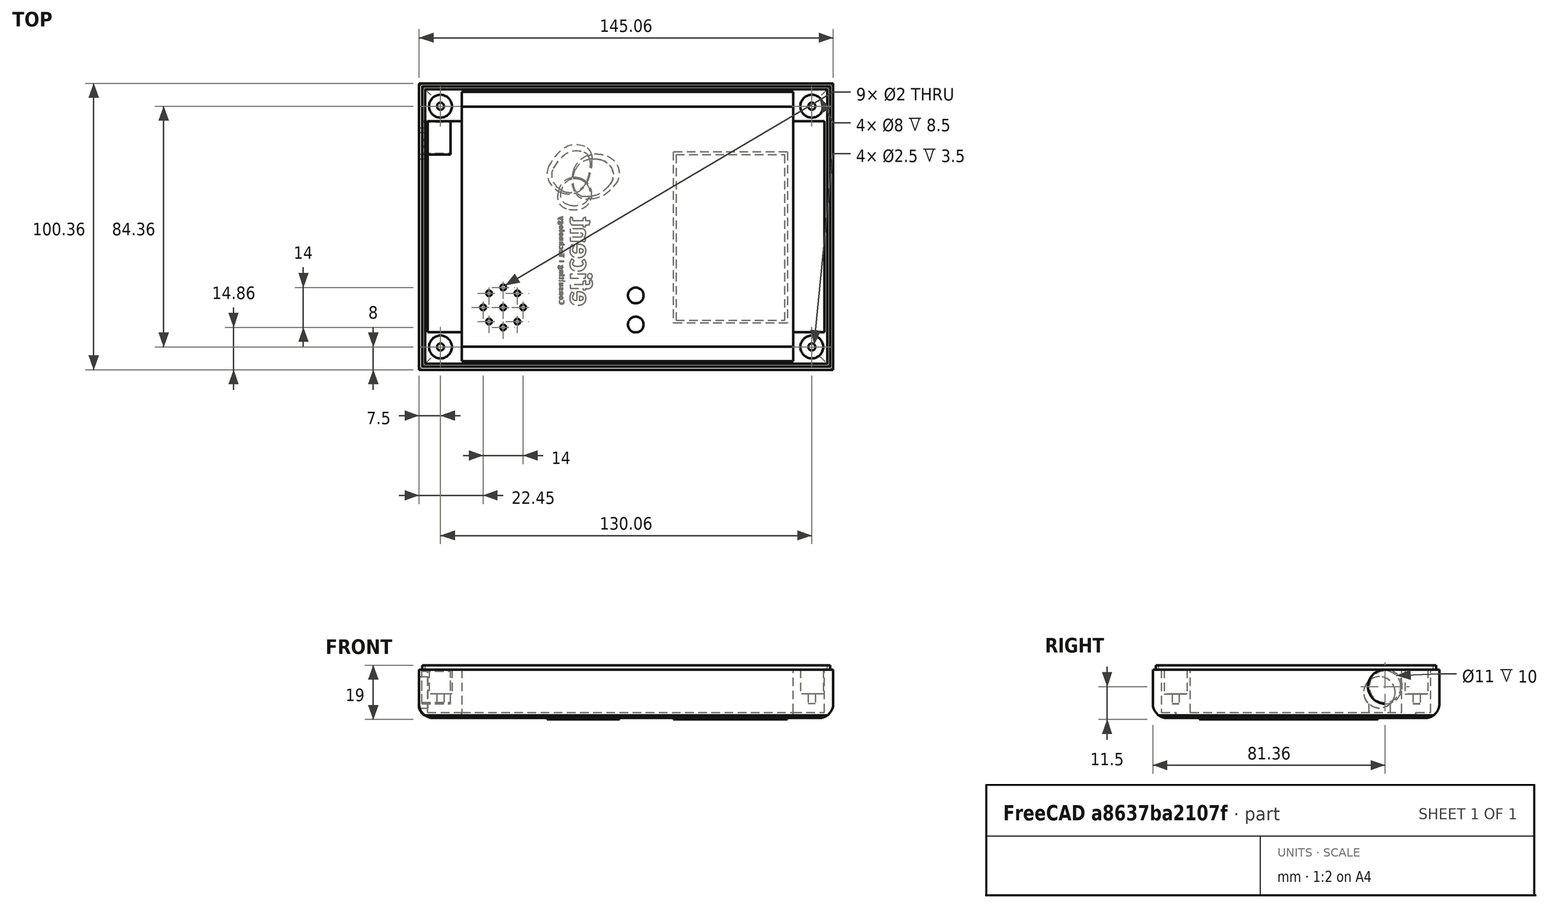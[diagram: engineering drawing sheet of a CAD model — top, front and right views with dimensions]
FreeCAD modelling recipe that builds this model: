
FCSTD DOCUMENT  (FreeCAD 0.16R6712 (Git))
Label: top_case_part1
License: All rights reserved
LicenseURL: http://en.wikipedia.org/wiki/All_rights_reserved
objects: Part::FeaturePython×63, Part::Extrusion×54, Part::Cut×48, Part::Box×31, Part::MultiFuse×27, Part::Cylinder×22, Part::Feature×5, Part::MultiCommon×3, Part::Fillet×2, App::MeasureDistance×1, Mesh::Feature×1
note: 255 computed .brp shape members not serialized (recipe doc carries the construction recipe); baked Part::Feature solids carry a one-line shape summary decoded from their .brp

FEATURE [Part::Box] Box005  label="top_case_master"
  Height = 17
  Length = 145.06
  Placement = pos=(-4,0,31) rot=(0,0,1;0rad)
  Width = 100.36
FEATURE [Part::Box] Box006  label="top_case_master_emptying"
  Height = 14
  Length = 116.06
  Placement = pos=(11,3,31) rot=(0,0,1;0rad)
  Width = 94.36
FEATURE [Part::Cut] Cut002  label="top_case_empty"
  Base = -> Box005
  Tool = -> Box006
FEATURE [Part::Cylinder] Cylinder002  label="hole_2_4"
  Angle = 360
  Height = 43
  Placement = pos=(3.5,8,0) rot=(0,0,1;0rad)
  Radius = 1.25
FEATURE [Part::FeaturePython] Array002  label="array_hole_2_4"  # Draft array (typed FeaturePython)
  Angle = 360
  ArrayType = 0
  Axis = (0,0,1)
  Base = -> Cylinder002
  Center = (0,0,0)
  Fuse = false
  IntervalAxis = (0,0,0)
  IntervalX = (130.06,0,0)
  IntervalY = (0,84.36,0)
  IntervalZ = (0,0,0)
  NumberPolar = 1
  NumberX = 2
  NumberY = 2
  NumberZ = 1
FEATURE [Part::Cut] Cut003  label="top_case_empty_witholes"
  Base = -> Cut002
  Tool = -> Array002
FEATURE [Part::Box] Box007  label="top_case_support_master"
  Height = 19.5
  Length = 7
  Placement = pos=(18.5,3,-10.5) rot=(0,0,1;0rad)
  Width = 7
FEATURE [Part::FeaturePython] Array003  label="array_top_case_support_master"  # Draft array (typed FeaturePython)
  Angle = 360
  ArrayType = 0
  Axis = (0,0,1)
  Base = -> Box007
  Center = (0,0,0)
  Fuse = false
  IntervalAxis = (0,0,0)
  IntervalX = (77.06,0,0)
  IntervalY = (0,87.36,0)
  IntervalZ = (0,0,0)
  NumberPolar = 1
  NumberX = 2
  NumberY = 2
  NumberZ = 1
  Placement = pos=(0,0,36) rot=(0,0,1;0rad)
FEATURE [Part::MultiFuse] Fusion004  label="top_case_withsupports"
  Placement = pos=(0,0,-16) rot=(0,0,1;0rad)
  Shapes = -> [Cut003,Array003]
FEATURE [Part::Cylinder] Cylinder003  label="hole_power_supply"
  Angle = 360
  Height = 19
  Placement = pos=(-5,21,23) rot=(0,1,0;1.5708rad)
  Radius = 5.5
FEATURE [Part::Cut] Cut004  label="top_case_with_power_supply_hole"
  Base = -> Fusion004
  Placement = pos=(0,0,21) rot=(0,0,1;0rad)
  Tool = -> Cylinder003
FEATURE [Part::Box] Box010  label="cierre_top_length_master"
  Height = 1.5
  Length = 142.76
  Placement = pos=(-2.9,1.1,34.5) rot=(0,0,1;0rad)
  Width = 1
FEATURE [Part::Box] Box011  label="cierre_top_width_master"
  Height = 1.5
  Length = 1
  Placement = pos=(-2.9,1.1,34.5) rot=(0,0,1;0rad)
  Width = 98.16
FEATURE [Part::FeaturePython] Array006  label="array_cierre_top_length"  # Draft array (typed FeaturePython)
  Angle = 360
  ArrayType = 0
  Axis = (0,0,1)
  Base = -> Box010
  Center = (0,0,0)
  Fuse = false
  IntervalAxis = (0,0,0)
  IntervalX = (1,0,0)
  IntervalY = (0,97.16,0)
  IntervalZ = (0,0,0)
  NumberPolar = 1
  NumberX = 1
  NumberY = 2
  NumberZ = 1
FEATURE [Part::FeaturePython] Array007  label="array_cierre_top_width"  # Draft array (typed FeaturePython)
  Angle = 360
  ArrayType = 0
  Axis = (0,0,1)
  Base = -> Box011
  Center = (0,0,0)
  Fuse = false
  IntervalAxis = (0,0,0)
  IntervalX = (141.86,0,0)
  IntervalY = (0,1,0)
  IntervalZ = (0,0,0)
  NumberPolar = 1
  NumberX = 2
  NumberY = 1
  NumberZ = 1
FEATURE [Part::MultiFuse] Fusion007
  Shapes = -> [Cut004,Array007]
FEATURE [Part::MultiFuse] Fusion008  label="top_case_with_border"
  Placement = pos=(0,0,2.5) rot=(0,0,1;0rad)
  Shapes = -> [Array006,Fusion007]
FEATURE [Part::Cylinder] Cylinder004  label="led2_hole_up"
  Angle = 360
  Height = 1
  Placement = pos=(71.9,84.5,52.5) rot=(0,0,1;0rad)
  Radius = 3
FEATURE [Part::Cylinder] Cylinder005  label="led1_hole_up"
  Angle = 360
  Height = 1
  Placement = pos=(71.9,74.3,52.5) rot=(0,0,1;0rad)
  Radius = 3
FEATURE [Part::Cut] Cut005
  Base = -> Fusion008
  Tool = -> Cylinder004
FEATURE [Part::Cut] Cut006  label="top_case_with_led_I"
  Base = -> Cut005
  Tool = -> Cylinder005
FEATURE [Part::Cylinder] Cylinder006  label="led1_hole_up001"
  Angle = 360
  Height = 4
  Placement = pos=(71.9,74.3,51.5) rot=(0,0,1;0rad)
  Radius = 2.75
FEATURE [Part::Cylinder] Cylinder007  label="led2_hole_up001"
  Angle = 360
  Height = 4
  Placement = pos=(71.9,84.5,51.5) rot=(0,0,1;0rad)
  Radius = 2.75
FEATURE [Part::Cut] Cut007
  Base = -> Cut006
  Tool = -> Cylinder006
FEATURE [Part::Cut] Cut008
  Base = -> Cut007
  Tool = -> Cylinder007
FEATURE [Part::Fillet] Fillet  label="top_case_bisel"
  Base = -> Cut008
  Edges = 4 edges r=5: [Edge2,Edge8,Edge9,Edge10]
FEATURE [Part::Box] Box012  label="slot_for_rfid"
  Height = 1
  Length = 40
  Placement = pos=(85,24,54.5) rot=(0,0,1;0rad)
  Width = 60
FEATURE [Part::Cut] Cut009  label="top_case_slot_rfid"
  Base = -> Fillet
  Tool = -> Box012
FEATURE [Part::Cylinder] Cylinder008  label="slot_for_buzzer"
  Angle = 360
  Height = 1
  Placement = pos=(39.4,79.4,54.5) rot=(0,0,1;0rad)
  Radius = 11
FEATURE [Part::Cylinder] Cylinder009  label="miniholes_buzzer_center"
  Angle = 360
  Height = 10
  Placement = pos=(25.446,78.5,49.5) rot=(0,0,1;0rad)
  Radius = 1
FEATURE [Part::Cylinder] Cylinder010  label="miniholes_buzzer_master"
  Angle = 360
  Height = 10
  Placement = pos=(18.45,78.5,49.5) rot=(0,0,1;0rad)
  Radius = 1
FEATURE [Part::FeaturePython] Array008  label="miniholes_buzzer_polar"  # Draft array (typed FeaturePython)
  Angle = 360
  ArrayType = 1
  Axis = (0,0,1)
  Base = -> Cylinder010
  Center = (25.45,78.5,49.5)
  Fuse = false
  IntervalAxis = (0,0,0)
  IntervalX = (1,0,0)
  IntervalY = (0,1,0)
  IntervalZ = (0,0,0)
  NumberPolar = 8
  NumberX = 2
  NumberY = 2
  NumberZ = 1
FEATURE [Part::MultiFuse] Fusion009
  Shapes = -> [Cut009,Cylinder008]
FEATURE [Part::Cut] Cut010
  Base = -> Fusion009
  Tool = -> Cylinder009
FEATURE [Part::Cut] Cut011  label="top_case_buzzer_holes"
  Base = -> Cut010
  Placement = pos=(0,0,-22) rot=(0,0,1;0rad)
  Tool = -> Array008
FEATURE [Part::Box] Box017  label="erase_supports_top"
  Height = 27.5
  Length = 100
  Placement = pos=(11,3,3) rot=(0,0,1;0rad)
  Width = 94.36
FEATURE [Part::Cut] Cut015  label="top_case_no_supports"
  Base = -> Cut011
  Tool = -> Box017
FEATURE [Part::Cylinder] Cylinder023  label="hole_2_005"
  Angle = 360
  Height = 25
  Placement = pos=(3.5,8,0) rot=(0,0,1;0rad)
  Radius = 4
FEATURE [Part::FeaturePython] Array027  label="array_hole_2_005"  # Draft array (typed FeaturePython)
  Angle = 360
  ArrayType = 0
  Axis = (0,0,1)
  Base = -> Cylinder023
  Center = (0,0,0)
  Fuse = false
  IntervalAxis = (0,0,0)
  IntervalX = (130.06,0,0)
  IntervalY = (0,84.36,0)
  IntervalZ = (0,0,0)
  NumberPolar = 1
  NumberX = 2
  NumberY = 2
  NumberZ = 1
FEATURE [Part::Cut] Cut024  label="top_case_nodiagonalprism"
  Base = -> Cut015
  Tool = -> Array027
FEATURE [Part::Box] Box018  label="slot_for_rfid_hole"
  Height = 5
  Length = 40
  Placement = pos=(85,24,29.5) rot=(0,0,1;0rad)
  Width = 60
FEATURE [Part::Cut] Cut
  Base = -> Cut024
  Tool = -> Box018
FEATURE [Part::Box] Box019  label="border_slot_rfid_short"
  Height = 1
  Length = 40
  Placement = pos=(85,23,32.5) rot=(0,0,1;0rad)
  Width = 2
FEATURE [Part::FeaturePython] Array  label="array_border_rfid_short"  # Draft array (typed FeaturePython)
  Angle = 360
  ArrayType = 0
  Axis = (0,0,1)
  Base = -> Box019
  Center = (0,0,0)
  Fuse = false
  IntervalAxis = (0,0,0)
  IntervalX = (1,0,0)
  IntervalY = (0,60,0)
  IntervalZ = (0,0,0)
  NumberPolar = 1
  NumberX = 1
  NumberY = 2
  NumberZ = 1
FEATURE [Part::Box] Box020  label="border_slot_rfid_large"
  Height = 1
  Length = 2
  Placement = pos=(84,24,32.5) rot=(0,0,1;0rad)
  Width = 60
FEATURE [Part::FeaturePython] Array028  label="array_border_rfid_large"  # Draft array (typed FeaturePython)
  Angle = 360
  ArrayType = 0
  Axis = (0,0,1)
  Base = -> Box020
  Center = (0,0,0)
  Fuse = false
  IntervalAxis = (0,0,0)
  IntervalX = (40,0,0)
  IntervalY = (0,1,0)
  IntervalZ = (0,0,0)
  NumberPolar = 1
  NumberX = 2
  NumberY = 1
  NumberZ = 1
FEATURE [Part::MultiFuse] Fusion  label="border_rfid_slot"
  Shapes = -> [Array028,Array]
FEATURE [Part::MultiFuse] Fusion010  label="top_case_3mm"
  Placement = pos=(6,103,34) rot=(1,0,0;3.14159rad)
  Shapes = -> [Cut,Fusion]
FEATURE [Part::Box] Box  label="Cube"
  Height = 10
  Length = 116.06
  Placement = pos=(17,5.64,1.5) rot=(0,0,1;0rad)
  Width = 94.36
FEATURE [Part::Cut] Cut025  label="top_case_finished"
  Base = -> Fusion010
  Tool = -> Box
FEATURE [Part::Box] Box021  label="Cube001"
  Height = 10
  Length = 147
  Placement = pos=(2,0,-8.5) rot=(0,0,1;0rad)
  Width = 105
FEATURE [Part::Cut] Cut026  label="top_case_base"
  Base = -> Cut025
  Tool = -> Box021
FEATURE [Part::Box] Box022  label="Cube002"
  Height = 20
  Length = 139
  Placement = pos=(5,15.8,0.5) rot=(0,0,1;0rad)
  Width = 74
FEATURE [App::MeasureDistance] Distance  label="Distance: 94,3623 mm"
  Distance = 94.3623
  P1 = (17,99.9746,17.5)
  P2 = (17.0065,5.61235,17.5)
FEATURE [Part::Cut] Cut027  label="top_case_part1"
  Base = -> Cut026
  Tool = -> Box022
FEATURE [Part::Box] Box023  label="big_rect"
  Height = 1
  Length = 116.06
  Placement = pos=(17,5.64,1.5) rot=(0,0,1;0rad)
  Width = 94.36
FEATURE [Part::Box] Box024  label="big_rect001"
  Height = 1
  Length = 139
  Placement = pos=(5,15.8,1.5) rot=(0,0,1;0rad)
  Width = 74
FEATURE [Part::Box] Box025  label="big_rect002"
  Height = 1
  Length = 116.06
  Placement = pos=(17,10.8,1.5) rot=(0,0,1;0rad)
  Width = 84
FEATURE [Part::Box] Box026  label="big_rect003"
  Height = 1
  Length = 139
  Placement = pos=(5,15.8,1.5) rot=(0,0,1;0rad)
  Width = 74
FEATURE [Part::MultiFuse] Fusion011
  Shapes = -> [Cut027,Box023]
FEATURE [Part::Cut] Cut028
  Base = -> Fusion011
  Tool = -> Box024
FEATURE [Part::MultiFuse] Fusion012
  Shapes = -> [Cut028,Box026]
FEATURE [Part::Box] Box027  label="top_case_master001"
  Height = 17
  Length = 145.06
  Placement = pos=(-4,0,31) rot=(0,0,1;0rad)
  Width = 100.36
FEATURE [Part::Box] Box028  label="top_case_master_emptying001"
  Height = 14
  Length = 116.06
  Placement = pos=(11,3,31) rot=(0,0,1;0rad)
  Width = 94.36
FEATURE [Part::Cut] Cut030  label="top_case_empty001"
  Base = -> Box027
  Tool = -> Box028
FEATURE [Part::Cylinder] Cylinder024  label="hole_2_006"
  Angle = 360
  Height = 43
  Placement = pos=(3.5,8,0) rot=(0,0,1;0rad)
  Radius = 1.25
FEATURE [Part::FeaturePython] Array029  label="array_hole_2_006"  # Draft array (typed FeaturePython)
  Angle = 360
  ArrayType = 0
  Axis = (0,0,1)
  Base = -> Cylinder024
  Center = (0,0,0)
  Fuse = false
  IntervalAxis = (0,0,0)
  IntervalX = (130.06,0,0)
  IntervalY = (0,84.36,0)
  IntervalZ = (0,0,0)
  NumberPolar = 1
  NumberX = 2
  NumberY = 2
  NumberZ = 1
FEATURE [Part::Cut] Cut031  label="top_case_empty_witholes001"
  Base = -> Cut030
  Tool = -> Array029
FEATURE [Part::Box] Box029  label="top_case_support_master001"
  Height = 19.5
  Length = 7
  Placement = pos=(18.5,3,-10.5) rot=(0,0,1;0rad)
  Width = 7
FEATURE [Part::FeaturePython] Array030  label="array_top_case_support_master001"  # Draft array (typed FeaturePython)
  Angle = 360
  ArrayType = 0
  Axis = (0,0,1)
  Base = -> Box029
  Center = (0,0,0)
  Fuse = false
  IntervalAxis = (0,0,0)
  IntervalX = (77.06,0,0)
  IntervalY = (0,87.36,0)
  IntervalZ = (0,0,0)
  NumberPolar = 1
  NumberX = 2
  NumberY = 2
  NumberZ = 1
  Placement = pos=(0,0,36) rot=(0,0,1;0rad)
FEATURE [Part::MultiFuse] Fusion013  label="top_case_withsupports001"
  Placement = pos=(0,0,-16) rot=(0,0,1;0rad)
  Shapes = -> [Cut031,Array030]
FEATURE [Part::Cylinder] Cylinder025  label="hole_power_supply001"
  Angle = 360
  Height = 19
  Placement = pos=(-5,19,21) rot=(0,1,0;1.5708rad)
  Radius = 5.5
FEATURE [Part::Cut] Cut032  label="top_case_with_power_supply_hole001"
  Base = -> Fusion013
  Placement = pos=(0,0,21) rot=(0,0,1;0rad)
  Tool = -> Cylinder025
FEATURE [Part::Box] Box030  label="cierre_top_length_master001"
  Height = 1.5
  Length = 143.06
  Placement = pos=(-3,1,34.5) rot=(0,0,1;0rad)
  Width = 1
FEATURE [Part::Box] Box031  label="cierre_top_width_master001"
  Height = 1.5
  Length = 1
  Placement = pos=(-3,1,34.5) rot=(0,0,1;0rad)
  Width = 98.36
FEATURE [Part::FeaturePython] Array031  label="array_cierre_top_length001"  # Draft array (typed FeaturePython)
  Angle = 360
  ArrayType = 0
  Axis = (0,0,1)
  Base = -> Box030
  Center = (0,0,0)
  Fuse = false
  IntervalAxis = (0,0,0)
  IntervalX = (1,0,0)
  IntervalY = (0,97.36,0)
  IntervalZ = (0,0,0)
  NumberPolar = 1
  NumberX = 1
  NumberY = 2
  NumberZ = 1
FEATURE [Part::FeaturePython] Array032  label="array_cierre_top_width001"  # Draft array (typed FeaturePython)
  Angle = 360
  ArrayType = 0
  Axis = (0,0,1)
  Base = -> Box031
  Center = (0,0,0)
  Fuse = false
  IntervalAxis = (0,0,0)
  IntervalX = (142.06,0,0)
  IntervalY = (0,1,0)
  IntervalZ = (0,0,0)
  NumberPolar = 1
  NumberX = 2
  NumberY = 1
  NumberZ = 1
FEATURE [Part::MultiFuse] Fusion014
  Shapes = -> [Cut032,Array032]
FEATURE [Part::MultiFuse] Fusion015  label="top_case_with_border001"
  Placement = pos=(0,0,2.5) rot=(0,0,1;0rad)
  Shapes = -> [Array031,Fusion014]
FEATURE [Part::Cylinder] Cylinder026  label="led2_hole_up002"
  Angle = 360
  Height = 1
  Placement = pos=(71.9,84.5,52.5) rot=(0,0,1;0rad)
  Radius = 3
FEATURE [Part::Cylinder] Cylinder027  label="led1_hole_up002"
  Angle = 360
  Height = 1
  Placement = pos=(71.9,74.3,52.5) rot=(0,0,1;0rad)
  Radius = 3
FEATURE [Part::Cut] Cut033
  Base = -> Fusion015
  Tool = -> Cylinder026
FEATURE [Part::Cut] Cut034  label="top_case_with_led_I001"
  Base = -> Cut033
  Tool = -> Cylinder027
FEATURE [Part::Cylinder] Cylinder028  label="led1_hole_up003"
  Angle = 360
  Height = 4
  Placement = pos=(71.9,74.3,51.5) rot=(0,0,1;0rad)
  Radius = 2.75
FEATURE [Part::Cylinder] Cylinder029  label="led2_hole_up003"
  Angle = 360
  Height = 4
  Placement = pos=(71.9,84.5,51.5) rot=(0,0,1;0rad)
  Radius = 2.75
FEATURE [Part::Cut] Cut035
  Base = -> Cut034
  Tool = -> Cylinder028
FEATURE [Part::Cut] Cut036
  Base = -> Cut035
  Tool = -> Cylinder029
FEATURE [Part::Fillet] Fillet001  label="top_case_bisel001"
  Base = -> Cut036
  Edges = 4 edges r=5: [Edge2,Edge8,Edge9,Edge10]
FEATURE [Part::Box] Box032  label="slot_for_rfid001"
  Height = 1
  Length = 40
  Placement = pos=(85,24,54.5) rot=(0,0,1;0rad)
  Width = 60
FEATURE [Part::Cut] Cut037  label="top_case_slot_rfid001"
  Base = -> Fillet001
  Tool = -> Box032
FEATURE [Part::Cylinder] Cylinder030  label="slot_for_buzzer001"
  Angle = 360
  Height = 1
  Placement = pos=(39.4,79.4,54.5) rot=(0,0,1;0rad)
  Radius = 11
FEATURE [Part::Cylinder] Cylinder031  label="miniholes_buzzer_center001"
  Angle = 360
  Height = 10
  Placement = pos=(25.446,78.5,49.5) rot=(0,0,1;0rad)
  Radius = 1
FEATURE [Part::Cylinder] Cylinder032  label="miniholes_buzzer_master001"
  Angle = 360
  Height = 10
  Placement = pos=(18.45,78.5,49.5) rot=(0,0,1;0rad)
  Radius = 1
FEATURE [Part::FeaturePython] Array033  label="miniholes_buzzer_polar001"  # Draft array (typed FeaturePython)
  Angle = 360
  ArrayType = 1
  Axis = (0,0,1)
  Base = -> Cylinder032
  Center = (25.45,78.5,49.5)
  Fuse = false
  IntervalAxis = (0,0,0)
  IntervalX = (1,0,0)
  IntervalY = (0,1,0)
  IntervalZ = (0,0,0)
  NumberPolar = 8
  NumberX = 2
  NumberY = 2
  NumberZ = 1
FEATURE [Part::MultiFuse] Fusion016
  Shapes = -> [Cut037,Cylinder030]
FEATURE [Part::Cut] Cut038
  Base = -> Fusion016
  Tool = -> Cylinder031
FEATURE [Part::Cut] Cut039  label="top_case_buzzer_holes001"
  Base = -> Cut038
  Placement = pos=(0,0,-22) rot=(0,0,1;0rad)
  Tool = -> Array033
FEATURE [Part::Box] Box033  label="erase_supports_top001"
  Height = 27.5
  Length = 100
  Placement = pos=(11,3,3) rot=(0,0,1;0rad)
  Width = 94.36
FEATURE [Part::Cut] Cut040  label="top_case_no_supports001"
  Base = -> Cut039
  Tool = -> Box033
FEATURE [Part::Cylinder] Cylinder033  label="hole_2_007"
  Angle = 360
  Height = 17
  Placement = pos=(3.5,8,0) rot=(0,0,1;0rad)
  Radius = 2.15
FEATURE [Part::FeaturePython] Array034  label="array_hole_2_007"  # Draft array (typed FeaturePython)
  Angle = 360
  ArrayType = 0
  Axis = (0,0,1)
  Base = -> Cylinder033
  Center = (0,0,0)
  Fuse = false
  IntervalAxis = (0,0,0)
  IntervalX = (130.06,0,0)
  IntervalY = (0,84.36,0)
  IntervalZ = (0,0,0)
  NumberPolar = 1
  NumberX = 2
  NumberY = 2
  NumberZ = 1
FEATURE [Part::Cut] Cut041  label="top_case_nodiagonalprism001"
  Base = -> Cut040
  Tool = -> Array034
FEATURE [Part::Box] Box034  label="slot_for_rfid_hole001"
  Height = 5
  Length = 40
  Placement = pos=(85,24,29.5) rot=(0,0,1;0rad)
  Width = 60
FEATURE [Part::Cut] Cut042
  Base = -> Cut041
  Tool = -> Box034
FEATURE [Part::Box] Box035  label="border_slot_rfid_short001"
  Height = 1
  Length = 40
  Placement = pos=(85,23,32.5) rot=(0,0,1;0rad)
  Width = 2
FEATURE [Part::FeaturePython] Array035  label="array_border_rfid_short001"  # Draft array (typed FeaturePython)
  Angle = 360
  ArrayType = 0
  Axis = (0,0,1)
  Base = -> Box035
  Center = (0,0,0)
  Fuse = false
  IntervalAxis = (0,0,0)
  IntervalX = (1,0,0)
  IntervalY = (0,60,0)
  IntervalZ = (0,0,0)
  NumberPolar = 1
  NumberX = 1
  NumberY = 2
  NumberZ = 1
FEATURE [Part::Box] Box036  label="border_slot_rfid_large001"
  Height = 1
  Length = 2
  Placement = pos=(84,24,32.5) rot=(0,0,1;0rad)
  Width = 60
FEATURE [Part::FeaturePython] Array036  label="array_border_rfid_large001"  # Draft array (typed FeaturePython)
  Angle = 360
  ArrayType = 0
  Axis = (0,0,1)
  Base = -> Box036
  Center = (0,0,0)
  Fuse = false
  IntervalAxis = (0,0,0)
  IntervalX = (40,0,0)
  IntervalY = (0,1,0)
  IntervalZ = (0,0,0)
  NumberPolar = 1
  NumberX = 2
  NumberY = 1
  NumberZ = 1
FEATURE [Part::MultiFuse] Fusion017  label="border_rfid_slot001"
  Shapes = -> [Array036,Array035]
FEATURE [Part::MultiFuse] Fusion018  label="top_case_3mm001"
  Placement = pos=(6,103,34) rot=(1,0,0;3.14159rad)
  Shapes = -> [Cut042,Fusion017]
FEATURE [Part::Box] Box037  label="Cube003"
  Height = 10
  Length = 116.06
  Placement = pos=(17,5.64,1.5) rot=(0,0,1;0rad)
  Width = 94.36
FEATURE [Part::Cut] Cut043  label="top_case_finished001"
  Base = -> Fusion018
  Tool = -> Box037
FEATURE [Part::Box] Box038  label="Cube004"
  Height = 20
  Length = 147
  Placement = pos=(2,0,1.5) rot=(0,0,1;0rad)
  Width = 105
FEATURE [Part::Cut] Cut044  label="top_case_norfidplace"
  Base = -> Cut043
  Placement = pos=(0,105,1.5) rot=(1,0,0;3.14159rad)
  Tool = -> Box038
FEATURE [Part::Box] Box039  label="rfid_place"
  Height = 1.5
  Length = 40
  Placement = pos=(91,26,0) rot=(0,0,1;0rad)
  Width = 60
FEATURE [Part::MultiFuse] Fusion019  label="top_case_rfidplacenohole"
  Shapes = -> [Cut044,Box039]
FEATURE [Part::Box] Box040  label="rfid_place001"
  Height = 0.5
  Length = 38
  Placement = pos=(92,27,1) rot=(0,0,1;0rad)
  Width = 58
FEATURE [Part::Cut] Cut045  label="top_case_part2_notext"
  Base = -> Fusion019
  Tool = -> Box040
FEATURE [Part::FeaturePython] Clone  label="t_eficent"  # WARN: FeaturePython — macro-defined, semantics opaque (R4)
  Scale = (0.35,0.35,0.35)
FEATURE [Part::FeaturePython] Clone001  label="n_eficent"  # WARN: FeaturePython — macro-defined, semantics opaque (R4)
  Scale = (0.35,0.35,0.35)
FEATURE [Part::FeaturePython] Clone002  label="second_e_out_eficent"  # WARN: FeaturePython — macro-defined, semantics opaque (R4)
  Scale = (0.35,0.35,0.35)
FEATURE [Part::FeaturePython] Clone003  label="second_e_in_eficent"  # WARN: FeaturePython — macro-defined, semantics opaque (R4)
  Scale = (0.35,0.35,0.35)
FEATURE [Part::FeaturePython] Clone004  label="c_eficent"  # WARN: FeaturePython — macro-defined, semantics opaque (R4)
  Scale = (0.35,0.35,0.35)
FEATURE [Part::FeaturePython] Clone005  label="dot_i_eficent"  # WARN: FeaturePython — macro-defined, semantics opaque (R4)
  Scale = (0.35,0.35,0.35)
FEATURE [Part::FeaturePython] Clone006  label="stick_i_eficent"  # WARN: FeaturePython — macro-defined, semantics opaque (R4)
  Scale = (0.35,0.35,0.35)
FEATURE [Part::FeaturePython] Clone007  label="f_eficent"  # WARN: FeaturePython — macro-defined, semantics opaque (R4)
  Scale = (0.35,0.35,0.35)
FEATURE [Part::FeaturePython] Clone008  label="first_e_out_eficent"  # WARN: FeaturePython — macro-defined, semantics opaque (R4)
  Scale = (0.35,0.35,0.35)
FEATURE [Part::FeaturePython] Clone009  label="first_e_in_eficent"  # WARN: FeaturePython — macro-defined, semantics opaque (R4)
  Scale = (0.35,0.35,0.35)
FEATURE [Part::FeaturePython] Clone010  label="y_technology"  # WARN: FeaturePython — macro-defined, semantics opaque (R4)
  Scale = (0.35,0.35,0.35)
FEATURE [Part::FeaturePython] Clone011  label="g_out_technology"  # WARN: FeaturePython — macro-defined, semantics opaque (R4)
  Scale = (0.35,0.35,0.35)
FEATURE [Part::FeaturePython] Clone012  label="g_in_technology"  # WARN: FeaturePython — macro-defined, semantics opaque (R4)
  Scale = (0.35,0.35,0.35)
FEATURE [Part::FeaturePython] Clone013  label="second_o_out_technology"  # WARN: FeaturePython — macro-defined, semantics opaque (R4)
  Scale = (0.35,0.35,0.35)
FEATURE [Part::FeaturePython] Clone014  label="first_o_in_technology"  # WARN: FeaturePython — macro-defined, semantics opaque (R4)
  Scale = (0.35,0.35,0.35)
FEATURE [Part::FeaturePython] Clone016  label="first_o_out_technology"  # WARN: FeaturePython — macro-defined, semantics opaque (R4)
  Scale = (0.35,0.35,0.35)
FEATURE [Part::FeaturePython] Clone017  label="first_o_in_technology001"  # WARN: FeaturePython — macro-defined, semantics opaque (R4)
  Scale = (0.35,0.35,0.35)
FEATURE [Part::FeaturePython] Clone018  label="n_technology"  # WARN: FeaturePython — macro-defined, semantics opaque (R4)
  Scale = (0.35,0.35,0.35)
FEATURE [Part::FeaturePython] Clone019  label="h_technology"  # WARN: FeaturePython — macro-defined, semantics opaque (R4)
  Scale = (0.35,0.35,0.35)
FEATURE [Part::FeaturePython] Clone020  label="c_technology"  # WARN: FeaturePython — macro-defined, semantics opaque (R4)
  Scale = (0.35,0.35,0.35)
FEATURE [Part::FeaturePython] Clone021  label="e_out_technology"  # WARN: FeaturePython — macro-defined, semantics opaque (R4)
  Scale = (0.35,0.35,0.35)
FEATURE [Part::FeaturePython] Clone022  label="e_in_technology"  # WARN: FeaturePython — macro-defined, semantics opaque (R4)
  Scale = (0.35,0.35,0.35)
FEATURE [Part::FeaturePython] Clone023  label="|"  # WARN: FeaturePython — macro-defined, semantics opaque (R4)
  Scale = (0.35,0.35,0.35)
FEATURE [Part::FeaturePython] Clone024  label="t_technology"  # WARN: FeaturePython — macro-defined, semantics opaque (R4)
  Scale = (0.35,0.35,0.35)
FEATURE [Part::FeaturePython] Clone025  label="g_in_consulting"  # WARN: FeaturePython — macro-defined, semantics opaque (R4)
  Scale = (0.35,0.35,0.35)
FEATURE [Part::FeaturePython] Clone026  label="g_out_consulting"  # WARN: FeaturePython — macro-defined, semantics opaque (R4)
  Scale = (0.35,0.35,0.35)
FEATURE [Part::FeaturePython] Clone027  label="dot_i_consulting"  # WARN: FeaturePython — macro-defined, semantics opaque (R4)
  Scale = (0.35,0.35,0.35)
FEATURE [Part::FeaturePython] Clone028  label="second_n_consulting"  # WARN: FeaturePython — macro-defined, semantics opaque (R4)
  Scale = (0.35,0.35,0.35)
FEATURE [Part::FeaturePython] Clone029  label="t_consulting"  # WARN: FeaturePython — macro-defined, semantics opaque (R4)
  Scale = (0.35,0.35,0.35)
FEATURE [Part::FeaturePython] Clone030  label="stick_i_consulting"  # WARN: FeaturePython — macro-defined, semantics opaque (R4)
  Scale = (0.35,0.35,0.35)
FEATURE [Part::FeaturePython] Clone031  label="u_consulting"  # WARN: FeaturePython — macro-defined, semantics opaque (R4)
  Scale = (0.35,0.35,0.35)
FEATURE [Part::FeaturePython] Clone032  label="l_consulting"  # WARN: FeaturePython — macro-defined, semantics opaque (R4)
  Scale = (0.35,0.35,0.35)
FEATURE [Part::FeaturePython] Clone033  label="first_n_consulting"  # WARN: FeaturePython — macro-defined, semantics opaque (R4)
  Scale = (0.35,0.35,0.35)
FEATURE [Part::FeaturePython] Clone034  label="s_consulting"  # WARN: FeaturePython — macro-defined, semantics opaque (R4)
  Scale = (0.35,0.35,0.35)
FEATURE [Part::FeaturePython] Clone035  label="o_out_consulting"  # WARN: FeaturePython — macro-defined, semantics opaque (R4)
  Scale = (0.35,0.35,0.35)
FEATURE [Part::FeaturePython] Clone036  label="o_in_consulting"  # WARN: FeaturePython — macro-defined, semantics opaque (R4)
  Scale = (0.35,0.35,0.35)
FEATURE [Part::FeaturePython] Clone038  label="c_consulting"  # WARN: FeaturePython — macro-defined, semantics opaque (R4)
  Scale = (0.35,0.35,0.35)
FEATURE [Part::Extrusion] Extrude
  Base = -> Clone
  Dir = (0,0,0.5)
  Placement = pos=(125,-26,1) rot=(0,0,-1;1.5708rad)
  Solid = true
FEATURE [Part::Extrusion] Extrude001
  Base = -> Clone001
  Dir = (0,0,0.5)
  Placement = pos=(125,-26,1) rot=(0,0,-1;1.5708rad)
  Solid = true
FEATURE [Part::Extrusion] Extrude002
  Base = -> Clone002
  Dir = (0,0,0.5)
  Solid = true
FEATURE [Part::Extrusion] Extrude003
  Base = -> Clone003
  Dir = (0,0,0.5)
  Solid = true
FEATURE [Part::Extrusion] Extrude004
  Base = -> Clone004
  Dir = (0,0,0.5)
  Placement = pos=(125,-26,1) rot=(0,0,-1;1.5708rad)
  Solid = true
FEATURE [Part::Extrusion] Extrude005
  Base = -> Clone005
  Dir = (0,0,0.5)
  Placement = pos=(125,-26,1) rot=(0,0,-1;1.5708rad)
  Solid = true
FEATURE [Part::Extrusion] Extrude006
  Base = -> Clone006
  Dir = (0,0,0.5)
  Placement = pos=(125,-26,1) rot=(0,0,-1;1.5708rad)
  Solid = true
FEATURE [Part::Extrusion] Extrude007
  Base = -> Clone007
  Dir = (0,0,0.5)
  Placement = pos=(125,-26,1) rot=(0,0,-1;1.5708rad)
  Solid = true
FEATURE [Part::Extrusion] Extrude008
  Base = -> Clone008
  Dir = (0,0,0.5)
  Solid = true
FEATURE [Part::Extrusion] Extrude009
  Base = -> Clone009
  Dir = (0,0,0.5)
  Solid = true
FEATURE [Part::Extrusion] Extrude010
  Base = -> Clone010
  Dir = (0,0,0.5)
  Placement = pos=(125,-26,1) rot=(0,0,-1;1.5708rad)
  Solid = true
FEATURE [Part::Extrusion] Extrude011
  Base = -> Clone011
  Dir = (0,0,0.5)
  Solid = true
FEATURE [Part::Extrusion] Extrude012
  Base = -> Clone012
  Dir = (0,0,0.5)
  Solid = true
FEATURE [Part::Extrusion] Extrude013
  Base = -> Clone013
  Dir = (0,0,0.5)
  Solid = true
FEATURE [Part::Extrusion] Extrude014
  Base = -> Clone014
  Dir = (0,0,0.5)
  Solid = true
FEATURE [Part::Extrusion] Extrude016
  Base = -> Clone016
  Dir = (0,0,0.5)
  Solid = true
FEATURE [Part::Extrusion] Extrude017
  Base = -> Clone017
  Dir = (0,0,0.5)
  Solid = true
FEATURE [Part::Extrusion] Extrude018
  Base = -> Clone018
  Dir = (0,0,0.5)
  Placement = pos=(125,-26,1) rot=(0,0,-1;1.5708rad)
  Solid = true
FEATURE [Part::Extrusion] Extrude019
  Base = -> Clone019
  Dir = (0,0,0.5)
  Placement = pos=(125,-26,1) rot=(0,0,-1;1.5708rad)
  Solid = true
FEATURE [Part::Extrusion] Extrude020
  Base = -> Clone020
  Dir = (0,0,0.5)
  Placement = pos=(125,-26,1) rot=(0,0,-1;1.5708rad)
  Solid = true
FEATURE [Part::Extrusion] Extrude021
  Base = -> Clone021
  Dir = (0,0,0.5)
  Solid = true
FEATURE [Part::Extrusion] Extrude022
  Base = -> Clone022
  Dir = (0,0,0.5)
  Solid = true
FEATURE [Part::Extrusion] Extrude023
  Base = -> Clone023
  Dir = (0,0,0.5)
  Placement = pos=(125,-26,1) rot=(0,0,-1;1.5708rad)
  Solid = true
FEATURE [Part::Extrusion] Extrude024
  Base = -> Clone024
  Dir = (0,0,0.5)
  Placement = pos=(125,-26,1) rot=(0,0,-1;1.5708rad)
  Solid = true
FEATURE [Part::Extrusion] Extrude025
  Base = -> Clone025
  Dir = (0,0,0.5)
  Solid = true
FEATURE [Part::Extrusion] Extrude026
  Base = -> Clone026
  Dir = (0,0,0.5)
  Solid = true
FEATURE [Part::Extrusion] Extrude027
  Base = -> Clone027
  Dir = (0,0,0.5)
  Placement = pos=(125,-26,1) rot=(0,0,-1;1.5708rad)
  Solid = true
FEATURE [Part::Extrusion] Extrude028
  Base = -> Clone028
  Dir = (0,0,0.5)
  Placement = pos=(125,-26,1) rot=(0,0,-1;1.5708rad)
  Solid = true
FEATURE [Part::Extrusion] Extrude029
  Base = -> Clone029
  Dir = (0,0,0.5)
  Placement = pos=(125,-26,1) rot=(0,0,-1;1.5708rad)
  Solid = true
FEATURE [Part::Extrusion] Extrude030
  Base = -> Clone030
  Dir = (0,0,0.5)
  Placement = pos=(125,-26,1) rot=(0,0,-1;1.5708rad)
  Solid = true
FEATURE [Part::Extrusion] Extrude031
  Base = -> Clone031
  Dir = (0,0,0.5)
  Placement = pos=(125,-26,1) rot=(0,0,-1;1.5708rad)
  Solid = true
FEATURE [Part::Extrusion] Extrude032
  Base = -> Clone032
  Dir = (0,0,0.75)
  Placement = pos=(125,-26,0.75) rot=(0,0,-1;1.5708rad)
  Solid = true
FEATURE [Part::Extrusion] Extrude033
  Base = -> Clone033
  Dir = (0,0,0.5)
  Placement = pos=(125,-26,1) rot=(0,0,-1;1.5708rad)
  Solid = true
FEATURE [Part::Extrusion] Extrude034
  Base = -> Clone034
  Dir = (0,0,0.5)
  Placement = pos=(125,-26,1) rot=(0,0,-1;1.5708rad)
  Solid = true
FEATURE [Part::Extrusion] Extrude035
  Base = -> Clone035
  Dir = (0,0,0.5)
  Solid = true
FEATURE [Part::Extrusion] Extrude036
  Base = -> Clone036
  Dir = (0,0,0.5)
  Solid = true
FEATURE [Part::Extrusion] Extrude037
  Base = -> Clone038
  Dir = (0,0,0.5)
  Placement = pos=(125,-26,1) rot=(0,0,-1;1.5708rad)
  Solid = true
FEATURE [Part::Cut] Cut046
  Base = -> Extrude035
  Placement = pos=(125,-26,1) rot=(0,0,-1;1.5708rad)
  Tool = -> Extrude036
FEATURE [Part::Cut] Cut047
  Base = -> Extrude026
  Placement = pos=(125,-26,1) rot=(0,0,-1;1.5708rad)
  Tool = -> Extrude025
FEATURE [Part::Cut] Cut048
  Base = -> Extrude021
  Placement = pos=(125,-26,1) rot=(0,0,-1;1.5708rad)
  Tool = -> Extrude022
FEATURE [Part::Cut] Cut049
  Base = -> Extrude016
  Placement = pos=(125,-26,1) rot=(0,0,-1;1.5708rad)
  Tool = -> Extrude017
FEATURE [Part::Cut] Cut050
  Base = -> Extrude013
  Placement = pos=(125,-26,1) rot=(0,0,-1;1.5708rad)
  Tool = -> Extrude014
FEATURE [Part::Cut] Cut051
  Base = -> Extrude011
  Placement = pos=(125,-26,1) rot=(0,0,-1;1.5708rad)
  Tool = -> Extrude012
FEATURE [Part::Cut] Cut052
  Base = -> Extrude008
  Placement = pos=(125,-26,1) rot=(0,0,-1;1.5708rad)
  Tool = -> Extrude009
FEATURE [Part::Cut] Cut053
  Base = -> Extrude002
  Placement = pos=(125,-26,1) rot=(0,0,-1;1.5708rad)
  Tool = -> Extrude003
FEATURE [Part::FeaturePython] Clone057  label="l_technology001"  # WARN: FeaturePython — macro-defined, semantics opaque (R4)
  Scale = (0.35,0.35,0.35)
FEATURE [Part::Extrusion] Extrude052
  Base = -> Clone057
  Dir = (0,0,0.75)
  Placement = pos=(125,-26,0.75) rot=(0,0,-1;1.5708rad)
  Solid = true
FEATURE [Part::MultiFuse] Fusion020
  Shapes = -> [Cut045,Cut050]
FEATURE [Part::MultiFuse] Fusion021
  Shapes = -> [Fusion020,Extrude]
FEATURE [Part::MultiFuse] Fusion022
  Shapes = -> [Fusion021,Extrude001,Extrude005]
FEATURE [Part::MultiFuse] Fusion023
  Shapes = -> [Fusion022,Extrude004,Extrude006,Extrude007]
FEATURE [Part::MultiFuse] Fusion024
  Shapes = -> [Cut052,Cut053,Fusion023]
FEATURE [Part::MultiFuse] Fusion025
  Shapes = -> [Fusion024,Cut049,Cut048,Cut046,Extrude020]
FEATURE [Part::MultiFuse] Fusion026
  Shapes = -> [Fusion025,Extrude027,Extrude030]
FEATURE [Part::MultiFuse] Fusion027
  Shapes = -> [Fusion026,Extrude034]
FEATURE [Part::MultiFuse] Fusion028
  Shapes = -> [Fusion027,Extrude037,Extrude024,Extrude023,Extrude033,Extrude019]
FEATURE [Part::MultiFuse] Fusion029
  Shapes = -> [Fusion028,Cut051,Cut047,Extrude032,Extrude031,Extrude029,Extrude028,Extrude018,Extrude010,Extrude052]
FEATURE [Part::FeaturePython] Clone084  label="Clone of path3100"  # WARN: FeaturePython — macro-defined, semantics opaque (R4)
  Placement = pos=(22.0938,-9.6665,0) rot=(0,0,1;0rad)
  Scale = (0.85,0.85,0.85)
FEATURE [Part::FeaturePython] Clone085  label="Clone of path3036"  # WARN: FeaturePython — macro-defined, semantics opaque (R4)
  Placement = pos=(22.0938,-9.6665,0) rot=(0,0,1;0rad)
  Scale = (0.85,0.85,0.85)
FEATURE [Part::FeaturePython] Clone086  label="Clone of path3052"  # WARN: FeaturePython — macro-defined, semantics opaque (R4)
  Placement = pos=(22.0938,-9.6665,0) rot=(0,0,1;0rad)
  Scale = (0.85,0.85,0.85)
FEATURE [Part::FeaturePython] Clone087  label="Clone of path3203"  # WARN: FeaturePython — macro-defined, semantics opaque (R4)
  Placement = pos=(22.0938,-9.6665,0) rot=(0,0,1;0rad)
  Scale = (0.85,0.85,0.85)
FEATURE [Part::Extrusion] Extrude082
  Dir = (0,0,1)
  Solid = true
FEATURE [Part::Extrusion] Extrude086
  Base = -> Clone087
  Dir = (0,0,1)
  Solid = true
FEATURE [Part::Feature] path3314002
  shape: bbox 44.54 x 34.74 x 2.5e-07 mm, 0 faces, 0 solids (baked)
FEATURE [Part::FeaturePython] Clone088  label="Clone of path3204"  # Draft clone (typed FeaturePython)
  Objects = -> [path3314002]
  Placement = pos=(22.0938,-9.6665,0) rot=(0,0,1;0rad)
  Scale = (0.85,0.85,0.85)
FEATURE [Part::Extrusion] Extrude087
  Base = -> path3314002
  Dir = (0,0,1)
  Solid = true
FEATURE [Part::Extrusion] Extrude088
  Base = -> Clone088
  Dir = (0,0,1)
  Solid = true
FEATURE [Part::MultiCommon] Common007
  Shapes = -> [Extrude087,Extrude088]
FEATURE [Part::Feature] path3314003
  shape: bbox 48.62 x 45.46 x 2.5e-07 mm, 0 faces, 0 solids (baked)
FEATURE [Part::FeaturePython] Clone089  label="Clone of path3205"  # Draft clone (typed FeaturePython)
  Objects = -> [path3314003]
  Placement = pos=(22.0938,-9.6665,0) rot=(0,0,1;0rad)
  Scale = (0.85,0.85,0.85)
FEATURE [Part::Extrusion] Extrude089
  Base = -> path3314003
  Dir = (0,0,1)
  Solid = true
FEATURE [Part::Extrusion] Extrude090
  Base = -> Clone089
  Dir = (0,0,1)
  Solid = true
FEATURE [Part::MultiCommon] Common008
  Shapes = -> [Extrude089,Extrude090]
FEATURE [Part::Feature] path3314004
  shape: bbox 19.47 x 34.66 x 2.5e-07 mm, 0 faces, 0 solids (baked)
FEATURE [Part::FeaturePython] Clone090  label="Clone of path3206"  # Draft clone (typed FeaturePython)
  Objects = -> [path3314004]
  Placement = pos=(22.0938,-9.6665,0) rot=(0,0,1;0rad)
  Scale = (0.85,0.85,0.85)
FEATURE [Part::Extrusion] Extrude091
  Base = -> path3314004
  Dir = (0,0,1)
  Solid = true
FEATURE [Part::Extrusion] Extrude092
  Base = -> Clone090
  Dir = (0,0,1)
  Solid = true
FEATURE [Part::Extrusion] Extrude080
  Dir = (0,0,1)
  Solid = true
FEATURE [Part::Extrusion] Extrude081
  Dir = (0,0,1)
  Solid = true
FEATURE [Part::Extrusion] Extrude079
  Dir = (0,0,1)
  Solid = true
FEATURE [Part::Cut] Cut054
  Base = -> Extrude082
  Tool = -> Extrude086
FEATURE [Part::Extrusion] Extrude093
  Base = -> Clone084
  Dir = (0,0,1)
  Solid = true
FEATURE [Part::Extrusion] Extrude094
  Base = -> Clone085
  Dir = (0,0,1)
  Solid = true
FEATURE [Part::Extrusion] Extrude095
  Base = -> Clone086
  Dir = (0,0,1)
  Solid = true
FEATURE [Part::Cut] Cut055
  Base = -> Extrude079
FEATURE [Part::Feature] path3314005
  shape: bbox 19.47 x 34.66 x 2.5e-07 mm, 0 faces, 0 solids (baked)
FEATURE [Part::FeaturePython] Clone091  label="Clone of path3207"  # Draft clone (typed FeaturePython)
  Objects = -> [path3314005]
  Placement = pos=(22.0938,-9.6665,0) rot=(0,0,1;0rad)
  Scale = (0.85,0.85,0.85)
FEATURE [Part::Extrusion] Extrude096
  Base = -> path3314005
  Dir = (0,0,1)
  Solid = true
FEATURE [Part::Extrusion] Extrude097
  Base = -> Clone091
  Dir = (0,0,1)
  Solid = true
FEATURE [Part::MultiCommon] Common010
  Shapes = -> [Extrude096,Extrude097]
FEATURE [Part::MultiFuse] Fusion035
  Shapes = -> [Extrude080,Extrude081,Cut054,Extrude093,Extrude095,Cut055,Extrude091,Extrude092,Extrude094]
FEATURE [Part::Cut] Cut056
  Base = -> Fusion035
  Tool = -> Common010
FEATURE [Part::Cut] Cut057
  Base = -> Cut056
  Tool = -> Common008
FEATURE [Part::Cut] Cut058
  Base = -> Cut057
  Tool = -> Common007
FEATURE [Part::FeaturePython] Scale  # Draft clone (typed FeaturePython)
  Objects = -> [Cut058]
  Placement = pos=(80.4987,88.8679,0.5) rot=(0,0,-1;1.5708rad)
  Scale = (0.35,0.35,1)
FEATURE [Part::MultiFuse] Fusion036  label="top_case_logo"
  Placement = pos=(0,105,1.5) rot=(1,0,0;3.14159rad)
  Shapes = -> [Fusion029,Scale]
FEATURE [Part::Cylinder] Cylinder
  Angle = 360
  Height = 10
  Placement = pos=(3,84,11.5) rot=(0,1,0;1.5708rad)
  Radius = 6
FEATURE [Part::Cylinder] Cylinder034
  Angle = 360
  Height = 10
  Placement = pos=(3,84,11.5) rot=(0,1,0;1.5708rad)
  Radius = 5.5
FEATURE [Part::Cut] Cut059
  Base = -> Cylinder
  Tool = -> Cylinder034
FEATURE [Part::Cut] Cut029
  Base = -> Fusion012
  Tool = -> Box025
FEATURE [Part::Feature] Cut029_solid  label="Cut029 (Solid)"
  shape: bbox 145.1 x 100.4 x 18.5 mm, 55 faces (baked)
FEATURE [Mesh::Feature] Mesh  label="Cut029 (Solid) (Meshed)"
